# Revit family: IS_Tempo_E1099_BIM_GB
name_source: partatom
category: Plumbing Fixtures
revit_build: Autodesk Revit MEP 2014 (Build: 20130308_1515(x64)
units: mm (PartAtom-declared; Revit-internal decimal feet)

## types (1)
- E109901 - Tempo 500mm Vanity Furniture Washbasin - Overflow - 1 Taphole
    Accessories = www.idealspec.co.uk
    AreaUnits = millimeters
    Assembly Code = C1030200
    AssetType = Fixed
    BIMObjectName = ISI_IdealStandard_CounterTopWashBasins_Tempo_E109901
    Brand = Ideal Standard
    CWFU = 0
    CeramicMtl = ISI_IdealStandard_Sanitaryware_Ceramic_White_Render
    Color = White
    ConnectionType = Plumbing
    Cost = 0 $
    Default Elevation = 0 mm  [stored 0 ft]
    Description = Tempo 50cm Vanity furniture washbasin, with overflow - one taphole
    DrainSize = 32 mm
    DurationUnit = year
    ECA = No
    ExpectedLife = 30
    Features = 50cm Vanity furniture washbasin, with overflow - one taphole
    Finish = White
    HWFU = 0
    IfcExportAs = IfcSanitaryType
    IfcExportType = WASHHANDBASIN
    InstallationInstructions = www.idealspec.co.uk/resources.html
    LinearUnits = millimeters
    ManufacturerURL = www.idealspec.co.uk
    Material = Vitreous china
    Model = E109901
    ModelNumber = E109901
    ModelReference = E109901
    NBSDescription = Countertop wash basins
    NBSReference = 45-35-70/360
    Name = CounterTopWashBasins_Tempo_E109901_IdealStandard
    NettWeight = 10 Kg
    NominalDepth = 105 mm  [stored 0.344488 ft]
    NominalHeight = 155 mm
    NominalLength = 500 mm
    NominalWidth = 450 mm
    ProductInformation = www.idealspec.co.uk/assets/datasheet/E109901
    Shape = Sculptured
    Size = 155 x 450 x 500 mm
    Space = Internal
    URL = www.idealspec.co.uk
    Uniclass2015Description = Counter top wash basins
    Uniclass2015Reference = Pr_40_20_96_18
    Uniclass2015Version = Products v1.1
    Version = 1
    VolumeUnits = Litres
    WFU = 0
    WRAS = No
    WarrantyDescription = Manufacturers Warranty
    WarrantyDurationParts = 99
    WarrantyDurationUnit = year
    WashHandBasinMounting = Counter top
    WashHandBasinType = Hand Rinse
    WaterEfficientProduct = No

note: [stored X ft] marks values corroborated as IEEE doubles in the binary element streams (Revit-internal decimal feet)

## geometry (parser evidence)
native form markers: Sweep x5
no freeform markers — native parametric forms only
